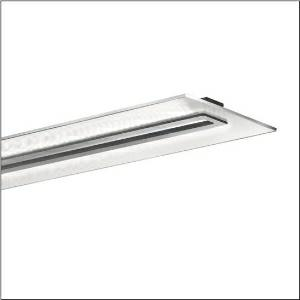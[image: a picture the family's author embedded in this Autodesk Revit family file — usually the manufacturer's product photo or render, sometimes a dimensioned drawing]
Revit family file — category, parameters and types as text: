
# Revit family: vega_r__11_5mn238dle_9bfa
name_source: partatom
category: Lighting Fixtures
units: mm (PartAtom-declared; Revit-internal decimal feet)

## family parameters
Cut with Voids When Loaded = No
Host = Face
Light Source = No
Part Type = Normal
Room Calculation Point = No
Round Connector Dimension = Use Diameter
Shared = No

## types (1)
- --- (1 x LED 4000K / CRI = 80, 8130 lm, 62 W, 4000K)
    Apparent Load = 62 VA
    Color Rendering = 83
    Color Temperature = 4000K
    Default Elevation = 1800 mm
    Description = Vega® 11, office luminaire, primary light control with prismatic reflector, of PMMA, transparent prismatic structure, CAT 2 (L<= 1500cd/m²), light emission: direct/indirect distribution, primary light characteristic: symmetric, installation type: suspended mounting, surface-mounted, LED rated luminous flux: 8.130 lm, light colour: 840, colour temperature: 4000K, control gear: ECG, with terminal, 3+2-pole, max. 2.5mm², mains connection: 230V, AC, 50Hz, connection cable inclusive, cable length: 1,5 m, rated input power: 62W, luminaire housing, rectangular, rounded, of aluminium section, anodised, metallic grey (RAL 9006), length: 1.250 mm, width: 350 mm, height: 43mm, luminaire housing, lower part, of aluminium section, anodised, metallic grey (RAL 9006), of PC, grey, protection rating (complete): IP20, insulation class (complete): insulation class I (protective earthing), certification: CE, standard: EN 50419, packaging unit: 1 piece
    Height = 40 mm  [stored 0.131234 ft]
    Lamp = 1 x LED 4000K / CRI >= 80
    Lamp Light Flux = 8130 lm
    Lamp Power = 62 W
    Lamp count = 1
    Length = 1250 mm
    Luminous efficacy = 0 lm/W
    Manufacturer = Siteco
    ModVariant = No
    Model = 5MN238DLE
    Mounting Place = Ceiling
    Mounting Type = Pendant
    Number of Poles = 1
    OnlyDefault = Yes
    Power Factor = 1
    Product Name = Vega® 11
    Product group = office luminaire | ceiling pendant
    ProductGroupID = 905
    Protection Class = Protection class I
    Protection Degree = IP 20
    RLX_Detail_Level = 1
    RlxData = <blob elided: 60661 chars, md5=60e8671d>
    Socket = socket
    Standby Power = 0 W
    System Light Flux = 0 lm
    System Power = 62 W
    Type Comments = factory setting: luminous flux: 100 % | dim-lin: 254 | 458 mA
    Type Image = l_1004807.jpg
    URL = http://relux.com
    VarID = @adj_147369
    Voltage = 0 V
    Weight = 0.00 kg
    Width = 350 mm

note: [stored X ft] marks values corroborated as IEEE doubles in the binary element streams (Revit-internal decimal feet)

## geometry (parser evidence)
native form markers: Blend x4, Sweep x10
no freeform markers — native parametric forms only
